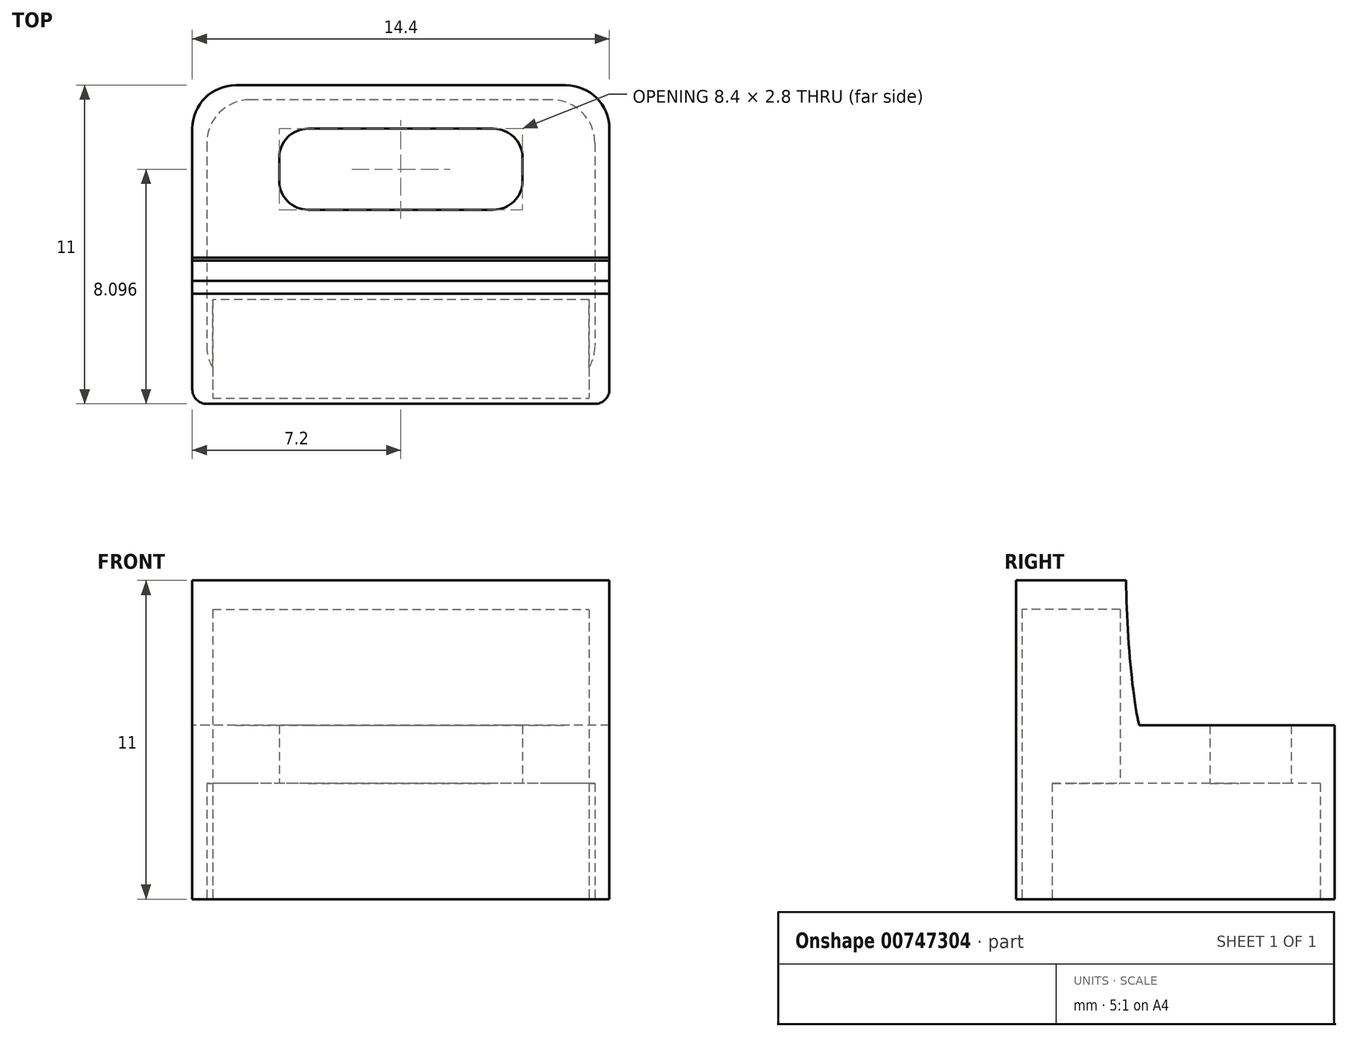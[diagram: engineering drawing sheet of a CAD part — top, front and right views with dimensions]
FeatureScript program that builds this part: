
annotation { "Feature Type Name" : "Feature", "Feature Type Description" : "" }
export const myFeature = defineFeature(function(context is Context, id is Id, definition is map)
    precondition{}
    {
        {
            var Q0;
            Q0=qCreatedBy(makeId("Top.planeOp"),FACE);
            var sketch = newSketch(context, id + "F0", { "sketchPlane" : qUnion([Q0])});
            skLineSegment(sketch, "E0.bottom", {"start": v(0.5, 2.88) * mm, "end": v(13.9, 2.88) * mm});
            skLineSegment(sketch, "E0.top", {"start": v(1.5, 13.88) * mm, "end": v(12.9, 13.88) * mm});
            skLineSegment(sketch, "E0.left", {"start": v(0, 3.38) * mm, "end": v(0, 12.38) * mm});
            skLineSegment(sketch, "E0.right", {"start": v(14.4, 3.38) * mm, "end": v(14.4, 12.38) * mm});
            skPoint(sketch, "E1.visualSharp", {"position": v(0, 13.88) * mm});
            skArc(sketch, "E1.filletArc", {"start": v(1.5, 13.88) * mm, "mid": v(0.44, 13.44) * mm, "end": v(0, 12.38) * mm});
            skPoint(sketch, "E2.visualSharp", {"position": v(14.4, 13.88) * mm});
            skArc(sketch, "E2.filletArc", {"start": v(14.4, 12.38) * mm, "mid": v(13.96, 13.44) * mm, "end": v(12.9, 13.88) * mm});
            skPoint(sketch, "E3.visualSharp", {"position": v(14.4, 2.88) * mm});
            skArc(sketch, "E3.filletArc", {"start": v(13.9, 2.88) * mm, "mid": v(14.25, 3.02) * mm, "end": v(14.4, 3.38) * mm});
            skPoint(sketch, "E4.visualSharp", {"position": v(0, 2.88) * mm});
            skArc(sketch, "E4.filletArc", {"start": v(0, 3.38) * mm, "mid": v(0.15, 3.02) * mm, "end": v(0.5, 2.88) * mm});
            skLineSegment(sketch, "E5.bottom", {"start": v(4, 12.38) * mm, "end": v(10.4, 12.38) * mm});
            skLineSegment(sketch, "E5.top", {"start": v(4, 9.58) * mm, "end": v(10.4, 9.58) * mm});
            skLineSegment(sketch, "E5.left", {"start": v(3, 11.38) * mm, "end": v(3, 10.58) * mm});
            skLineSegment(sketch, "E5.right", {"start": v(11.4, 11.38) * mm, "end": v(11.4, 10.58) * mm});
            skPoint(sketch, "E6.visualSharp", {"position": v(3, 12.38) * mm});
            skArc(sketch, "E6.filletArc", {"start": v(4, 12.38) * mm, "mid": v(3.3, 12.08) * mm, "end": v(3, 11.38) * mm});
            skPoint(sketch, "E7.visualSharp", {"position": v(3, 9.58) * mm});
            skArc(sketch, "E7.filletArc", {"start": v(3, 10.58) * mm, "mid": v(3.3, 9.87) * mm, "end": v(4, 9.58) * mm});
            skPoint(sketch, "E8.visualSharp", {"position": v(11.4, 12.38) * mm});
            skArc(sketch, "E8.filletArc", {"start": v(11.4, 11.38) * mm, "mid": v(11.1, 12.08) * mm, "end": v(10.4, 12.38) * mm});
            skPoint(sketch, "E9.visualSharp", {"position": v(11.4, 9.58) * mm});
            skArc(sketch, "E9.filletArc", {"start": v(10.4, 9.58) * mm, "mid": v(11.1, 9.87) * mm, "end": v(11.4, 10.58) * mm});
            skLineSegment(sketch, "E10", {"start": v(0, 3.38) * mm, "end": v(14.4, 3.38) * mm});
            skSolve(sketch);
        }
        {
            var Q0;
            Q0=qSketchRegion(id+"F0",true);
            extrude(context, id + "F1", {"entities" : qUnion([Q0]), "depth" : 6 * mm, "offsetDistance" : 25 * mm});
        }
        {
            var Q0;
            Q0=qCreatedBy(makeId("Top.planeOp"),FACE);
            var sketch = newSketch(context, id + "F2", { "sketchPlane" : qUnion([Q0])});
            skLineSegment(sketch, "E11.bottom", {"start": v(12.4, 13.38) * mm, "end": v(2, 13.38) * mm});
            skLineSegment(sketch, "E11.top", {"start": v(12.4, 3.38) * mm, "end": v(2, 3.38) * mm});
            skLineSegment(sketch, "E11.left", {"start": v(13.9, 11.88) * mm, "end": v(13.9, 4.88) * mm});
            skLineSegment(sketch, "E11.right", {"start": v(0.5, 11.88) * mm, "end": v(0.5, 4.88) * mm});
            skLineSegment(sketch, "E12.bottom", {"start": v(14.5, 3.38) * mm, "end": v(27, 3.38) * mm});
            skPoint(sketch, "E13.visualSharp", {"position": v(0.5, 3.38) * mm});
            skArc(sketch, "E13.filletArc", {"start": v(0.5, 4.88) * mm, "mid": v(0.94, 3.82) * mm, "end": v(2, 3.38) * mm});
            skPoint(sketch, "E14.visualSharp", {"position": v(0.5, 13.38) * mm});
            skArc(sketch, "E14.filletArc", {"start": v(2, 13.38) * mm, "mid": v(0.94, 12.94) * mm, "end": v(0.5, 11.88) * mm});
            skPoint(sketch, "E15.visualSharp", {"position": v(13.9, 13.38) * mm});
            skArc(sketch, "E15.filletArc", {"start": v(13.9, 11.88) * mm, "mid": v(13.46, 12.94) * mm, "end": v(12.4, 13.38) * mm});
            skPoint(sketch, "E16.visualSharp", {"position": v(13.9, 3.38) * mm});
            skArc(sketch, "E16.filletArc", {"start": v(12.4, 3.38) * mm, "mid": v(13.46, 3.82) * mm, "end": v(13.9, 4.88) * mm});
            skSolve(sketch);
        }
        {
            var Q0;
            Q0=qSketchRegion(id+"F2",true);
            extrude(context, id + "F3", {"entities" : qUnion([Q0]), "operationType" : NewBodyOperationType.REMOVE, "depth" : 4 * mm, "offsetDistance" : 25 * mm});
        }
        {
            var Q0;
            Q0=makeQuery(id+"F1.opExtrude","CAP_FACE",FACE,{"disambiguationData":[OSD([sQuery(id+"F0.wireOp",EDGE,"E0.bottom"),sQuery(id+"F0.wireOp",EDGE,"E0.top"),sQuery(id+"F0.wireOp",EDGE,"E0.left"),sQuery(id+"F0.wireOp",EDGE,"E0.right"),sQuery(id+"F0.wireOp",EDGE,"E1.filletArc"),sQuery(id+"F0.wireOp",EDGE,"E2.filletArc"),sQuery(id+"F0.wireOp",EDGE,"E3.filletArc"),sQuery(id+"F0.wireOp",EDGE,"E4.filletArc"),sQuery(id+"F0.wireOp",EDGE,"E5.bottom"),sQuery(id+"F0.wireOp",EDGE,"E5.top"),sQuery(id+"F0.wireOp",EDGE,"E5.left"),sQuery(id+"F0.wireOp",EDGE,"E5.right"),sQuery(id+"F0.wireOp",EDGE,"E6.filletArc"),sQuery(id+"F0.wireOp",EDGE,"E7.filletArc"),sQuery(id+"F0.wireOp",EDGE,"E8.filletArc"),sQuery(id+"F0.wireOp",EDGE,"E9.filletArc")])],"isStart":false});
            var sketch = newSketch(context, id + "F4", { "sketchPlane" : qUnion([Q0])});
            skLineSegment(sketch, "E17.bottom", {"start": v(0, 6.68) * mm, "end": v(14.4, 6.68) * mm});
            skLineSegment(sketch, "E17.top", {"start": v(0.5, 2.88) * mm, "end": v(13.9, 2.88) * mm});
            skLineSegment(sketch, "E17.left", {"start": v(0, 6.68) * mm, "end": v(0, 3.38) * mm});
            skLineSegment(sketch, "E17.right", {"start": v(14.4, 6.68) * mm, "end": v(14.4, 3.38) * mm});
            skPoint(sketch, "E18.visualSharp", {"position": v(0, 2.88) * mm});
            skArc(sketch, "E18.filletArc", {"start": v(0, 3.38) * mm, "mid": v(0.15, 3.02) * mm, "end": v(0.5, 2.88) * mm});
            skPoint(sketch, "E19.visualSharp", {"position": v(14.4, 2.88) * mm});
            skArc(sketch, "E19.filletArc", {"start": v(13.9, 2.88) * mm, "mid": v(14.25, 3.02) * mm, "end": v(14.4, 3.38) * mm});
            skSolve(sketch);
        }
        {
            var Q0;
            Q0 = qSketchRegion(id + "F4", true);
            var Q1;
            Q1=makeQuery(id+"F4.imprint","IMPRINT",FACE,{"disambiguationData":[TD([[makeQuery(id+"F4.imprint","IMPRINT",EDGE,{"derivedFrom":sQuery(id+"F4.wireOp",EDGE,"t1TrR9jy-unnC-8Y5A-bCdn-mWMWzz47JNdE")}),1.0]])]});
            extrude(context, id + "F5", {"entities" : qUnion([Q0, Q1]), "operationType" : NewBodyOperationType.ADD, "depth" : 5 * mm, "offsetDistance" : 25 * mm});
        }
        {
            var Q0;
            Q0=makeQuery(id+"F1.opExtrude","CAP_FACE",FACE,{"disambiguationData":[OSD([sQuery(id+"F0.wireOp",EDGE,"E0.bottom"),sQuery(id+"F0.wireOp",EDGE,"E0.top"),sQuery(id+"F0.wireOp",EDGE,"E0.left"),sQuery(id+"F0.wireOp",EDGE,"E0.right"),sQuery(id+"F0.wireOp",EDGE,"E1.filletArc"),sQuery(id+"F0.wireOp",EDGE,"E2.filletArc"),sQuery(id+"F0.wireOp",EDGE,"E3.filletArc"),sQuery(id+"F0.wireOp",EDGE,"E4.filletArc"),sQuery(id+"F0.wireOp",EDGE,"E5.bottom"),sQuery(id+"F0.wireOp",EDGE,"E5.top"),sQuery(id+"F0.wireOp",EDGE,"E5.left"),sQuery(id+"F0.wireOp",EDGE,"E5.right"),sQuery(id+"F0.wireOp",EDGE,"E6.filletArc"),sQuery(id+"F0.wireOp",EDGE,"E7.filletArc"),sQuery(id+"F0.wireOp",EDGE,"E8.filletArc"),sQuery(id+"F0.wireOp",EDGE,"E9.filletArc")])],"isStart":true});
            var sketch = newSketch(context, id + "F6", { "sketchPlane" : qUnion([Q0])});
            skLineSegment(sketch, "E20.bottom", {"start": v(0.7, -6.48) * mm, "end": v(13.7, -6.48) * mm});
            skLineSegment(sketch, "E20.top", {"start": v(0.7, -3.08) * mm, "end": v(13.7, -3.08) * mm});
            skLineSegment(sketch, "E20.left", {"start": v(0.7, -6.48) * mm, "end": v(0.7, -3.08) * mm});
            skLineSegment(sketch, "E20.right", {"start": v(13.7, -6.48) * mm, "end": v(13.7, -3.08) * mm});
            skSolve(sketch);
        }
        {
            var Q0;
            Q0 = qSketchRegion(id + "F6", true);
            extrude(context, id + "F7", {"entities" : qUnion([Q0]), "operationType" : NewBodyOperationType.REMOVE, "oppositeDirection" : true, "depth" : 10 * mm, "offsetDistance" : 25 * mm});
        }
        {
            var Q0;
            Q0=qCreatedBy(makeId("Right.planeOp"),FACE);
            var sketch = newSketch(context, id + "F8", { "sketchPlane" : qUnion([Q0])});
            skLineSegment(sketch, "E21", {"start": v(6.68, 11) * mm, "end": v(6.68, 6) * mm});
            skPoint(sketch, "E22.1.internal.snap0", {"position": v(7.93, 6) * mm});
            skFitSpline(sketch, "E23", {"points": [v(7.93, 6) * mm, v(7.41, 5.49) * mm, v(6.68, 11) * mm], "startDerivative": vector(-2.78, 0.88) * mm, "endDerivative": vector(-0.1, 9.83) * mm});
            skLineSegment(sketch, "E24", {"start": v(6.68, 6) * mm, "end": v(7.93, 6) * mm});
            skSolve(sketch);
        }
        {
            var Q0;
            Q0 = qSketchRegion(id + "F8", true);
            extrude(context, id + "F9", {"entities" : qUnion([Q0]), "operationType" : NewBodyOperationType.ADD, "depth" : 14.4 * mm, "offsetDistance" : 25 * mm});
        }
    });
